# Revit family: Control_Panels-Lutron-DIN_Rail_Panel_Enclosure-Satellite_Panel
name_source: partatom
category: Electrical Equipment
revit_build: Autodesk Revit 2018 (Build: 20170223_1515(x64)
units: mm (PartAtom-declared; Revit-internal decimal feet)

## family parameters
Cut with Voids When Loaded = No
Host = Face
OmniClass Number = 23.80.30.11.17
OmniClass Title = Distribution Boards and Control Panels
Panel Configuration = Two Columns, Circuits Across
Part Type = Panelboard
Room Calculation Point = No
Round Connector Dimension = Use Radius
Shared = No

## types (3) — shared parameters
Assembly Code = D5020
Breaker Panel Note (Hover Over Value) = – 120/240 V~ 50/60 Hz (single phase 3-wire)
– 120/208 V~ 50/60 Hz (three phase 4-wire)
– 15 A or 20 A branch breakers
– 125 A main lugs
Description = Athena QS DIN Rail Panel
Electrical Potential = 120 V
Feed Through Control Circuit Voltage = 120 V
Feed Through Note = 120/277 V~ 50/60 Hz 20 A max per circuit
Finish = Steel - Lutron - Black
Frequency = 50 Hz
Ground Bus = Yes
Instruction Sheet Link = http://www.lutron.com
Load Classification = Power
MCB Rating = 1 A
Manufacturer = Lutron Electronics Co., Inc
Manufacturer Fax Number = 610-282-1243
Neutral Bus = Yes
Neutral Rating = 0.00%
Number of Poles = 1
Overall Depth = 3.94 "
Overall Width = 15.875 "
Performance URL = http://www.lutron.com
Phase = 1
Power Factor = 1
Product Documentation Link = https://www.lutron.com
Product Name = DIN Rail Panel
Product Page URL = https://www.lutron.com
Series = Athena
SubFeed Lugs = No
URL = http://www.lutron.com
Unit Weight = 0.00 lb
Version = 2018 - v1.0a
Video Link = https://www.youtube.com
Voltage = 120.00 V
Warranty URL = http://www.lutron.com
zero-valued in all types: Cost, Default Elevation

## per-type parameters (varying)
| type | 16 Panel Size | 42 Panel Size | 65 Panel Size | Electrical Connector Distance | Overall Height |
| PD2-S-ASM | Yes | No | No | 16 " | 16 " |
| PD6-S-ASM | No | Yes | No | 42 " | 42 " |
| PD10-S-ASM | No | No | Yes | 65 " | 65 " |

note: column(s) folded — value = type name in every type: Model

## geometry (parser evidence)
native form markers: Sweep x2
no freeform markers — native parametric forms only
